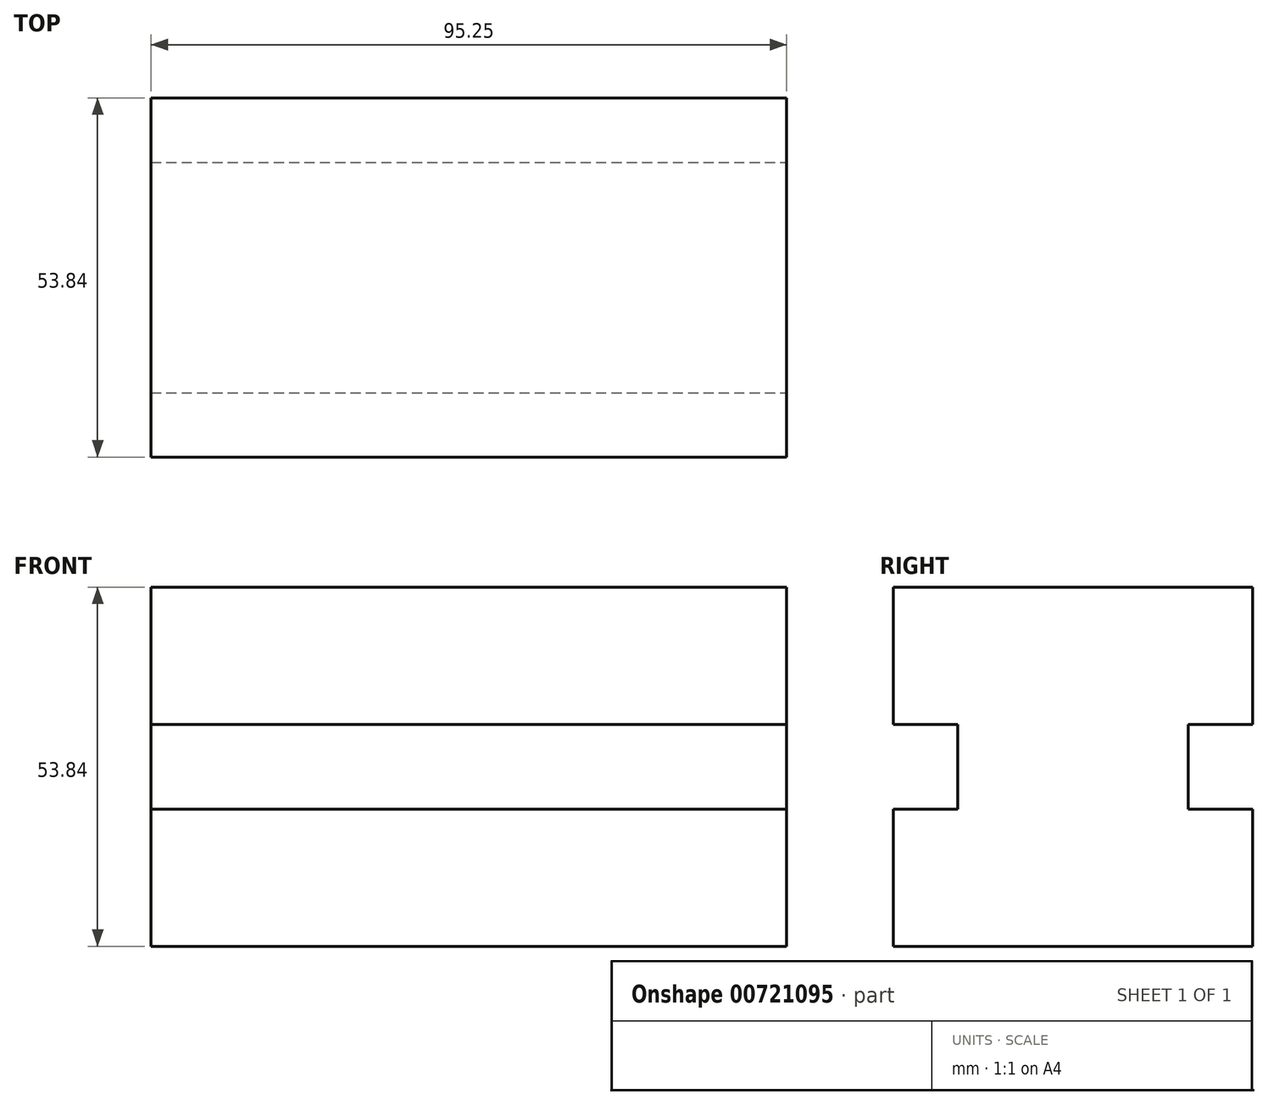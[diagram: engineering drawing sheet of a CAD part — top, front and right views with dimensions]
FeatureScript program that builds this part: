
annotation { "Feature Type Name" : "Feature", "Feature Type Description" : "" }
export const myFeature = defineFeature(function(context is Context, id is Id, definition is map)
    precondition{}
    {
        {
            var Q0;
            Q0=qCreatedBy(makeId("Right.planeOp"),FACE);
            var sketch = newSketch(context, id + "F0", { "sketchPlane" : qUnion([Q0])});
            skLineSegment(sketch, "E0.bottom", {"start": v(26.92, -26.92) * mm, "end": v(-26.92, -26.92) * mm});
            skLineSegment(sketch, "E0.top", {"start": v(26.92, 26.92) * mm, "end": v(-26.92, 26.92) * mm});
            skLineSegment(sketch, "E0.left", {"start": v(26.92, -26.92) * mm, "end": v(26.92, -6.35) * mm});
            skLineSegment(sketch, "E0.right", {"start": v(-26.92, -26.92) * mm, "end": v(-26.92, -6.35) * mm});
            skPoint(sketch, "E0.middle", {"position": v(0, 0) * mm});
            skLineSegment(sketch, "E1.bottom", {"start": v(-26.92, 6.35) * mm, "end": v(-17.27, 6.35) * mm});
            skLineSegment(sketch, "E1.top", {"start": v(-26.92, -6.35) * mm, "end": v(-17.27, -6.35) * mm});
            skLineSegment(sketch, "E1.right", {"start": v(-17.27, 6.35) * mm, "end": v(-17.27, -6.35) * mm});
            skLineSegment(sketch, "E2", {"start": v(0, 30.9) * mm, "end": v(0, -30.51) * mm, "construction": true});
            skLineSegment(sketch, "E3.MirrorCS", {"start": v(26.92, 6.35) * mm, "end": v(17.27, 6.35) * mm});
            skLineSegment(sketch, "E4.MirrorCS", {"start": v(17.27, 6.35) * mm, "end": v(17.27, -6.35) * mm});
            skLineSegment(sketch, "E5.MirrorCS", {"start": v(26.92, -6.35) * mm, "end": v(17.27, -6.35) * mm});
            skLineSegment(sketch, "E6.trimOffspring", {"start": v(-26.92, 6.35) * mm, "end": v(-26.92, 26.92) * mm});
            skLineSegment(sketch, "E7.trimOffspring", {"start": v(26.92, 6.35) * mm, "end": v(26.92, 26.92) * mm});
            skSolve(sketch);
        }
        {
            var Q0;
            Q0=makeQuery(id+"F0.imprint","IMPRINT",FACE,{"disambiguationData":[TD([[makeQuery(id+"F0.imprint","IMPRINT",EDGE,{"derivedFrom":sQuery(id+"F0.wireOp",EDGE,"E0.bottom")}),-1.0]])]});
            extrude(context, id + "F1", {"entities" : qUnion([Q0]), "oppositeDirection" : true, "depth" : 95.25 * mm, "offsetDistance" : 25.4 * mm});
        }
    });
